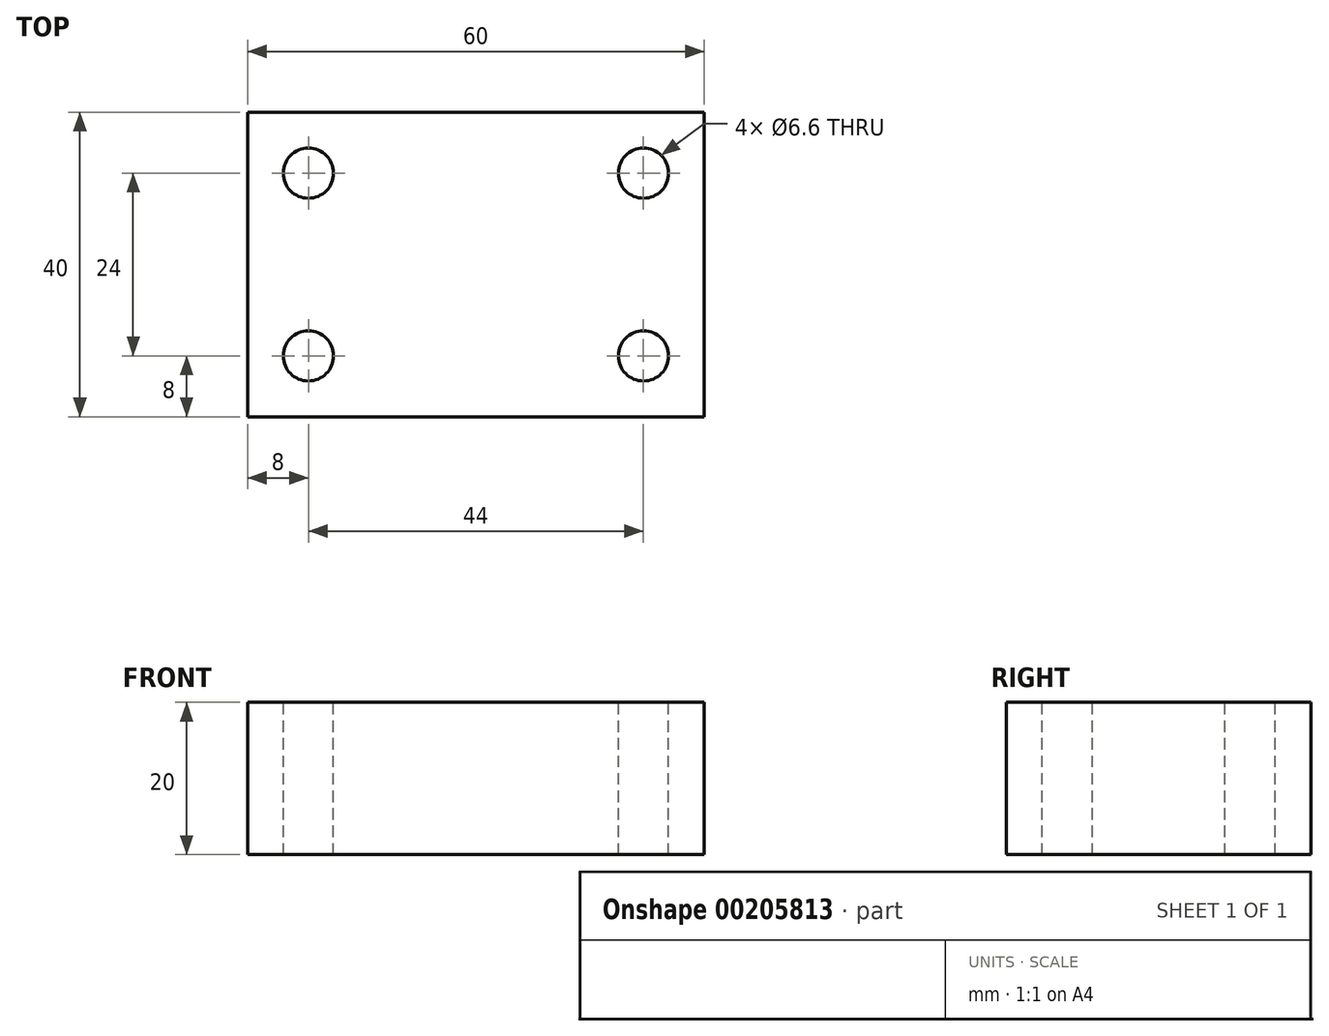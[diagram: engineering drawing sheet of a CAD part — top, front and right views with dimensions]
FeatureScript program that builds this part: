
annotation { "Feature Type Name" : "Feature", "Feature Type Description" : "" }
export const myFeature = defineFeature(function(context is Context, id is Id, definition is map)
    precondition{}
    {
        {
            var Q0;
            Q0=qCreatedBy(makeId("Top.planeOp"),FACE);
            var sketch = newSketch(context, id + "F0", { "sketchPlane" : qUnion([Q0])});
            skLineSegment(sketch, "E0.bottom", {"start": v(15, 10) * mm, "end": v(-15, 10) * mm});
            skLineSegment(sketch, "E0.top", {"start": v(15, -10) * mm, "end": v(-15, -10) * mm});
            skLineSegment(sketch, "E0.left", {"start": v(15, 10) * mm, "end": v(15, -10) * mm});
            skLineSegment(sketch, "E0.right", {"start": v(-15, 10) * mm, "end": v(-15, -10) * mm});
            skPoint(sketch, "E0.middle", {"position": v(0, 0) * mm});
            skSolve(sketch);
        }
        {
            var Q0;
            Q0=makeQuery(id+"F0.imprint","IMPRINT",FACE,{"disambiguationData":[TD([[makeQuery(id+"F0.imprint","IMPRINT",EDGE,{"derivedFrom":sQuery(id+"F0.wireOp",EDGE,"E0.bottom")}),1.0]])]});
            extrude(context, id + "F1", {"entities" : qUnion([Q0]), "depth" : 20 * mm});
        }
        {
            var Q0;
            Q0=makeQuery(id+"F1.opExtrude","CAP_FACE",FACE,{"disambiguationData":[OSD([sQuery(id+"F0.wireOp",EDGE,"E0.bottom"),sQuery(id+"F0.wireOp",EDGE,"E0.top"),sQuery(id+"F0.wireOp",EDGE,"E0.left"),sQuery(id+"F0.wireOp",EDGE,"E0.right")])],"isStart":false});
            var sketch = newSketch(context, id + "F2", { "sketchPlane" : qUnion([Q0])});
            skPoint(sketch, "E1", {"position": v(-7, 2) * mm});
            skSolve(sketch);
        }
        {
            var Q0;
            Q0=sQuery(id+"F2.wireOp",VERTEX,"E1");
            var Q1;
            Q1=makeQuery(id+"F1.opExtrude","SWEPT_BODY",BODY,{"disambiguationData":[OSD([sQuery(id+"F0.wireOp",EDGE,"E0.bottom"),sQuery(id+"F0.wireOp",EDGE,"E0.top"),sQuery(id+"F0.wireOp",EDGE,"E0.left"),sQuery(id+"F0.wireOp",EDGE,"E0.right")])]});
            hole(context, id + "F3", {"style" : HoleStyle.SIMPLE, "endStyle" : HoleEndStyle.THROUGH, "holeDiameter" : 6.6 * mm, "locations" : qUnion([Q0]), "scope" : qUnion([Q1]), "isTappedThrough" : true});
        }
        {
            var Q0;
            Q0=makeQuery(id+"F1.opExtrude","SWEPT_BODY",BODY,{"disambiguationData":[OSD([sQuery(id+"F0.wireOp",EDGE,"E0.bottom"),sQuery(id+"F0.wireOp",EDGE,"E0.top"),sQuery(id+"F0.wireOp",EDGE,"E0.left"),sQuery(id+"F0.wireOp",EDGE,"E0.right")])]});
            var Q1;
            Q1=makeQuery(id+"F1.opExtrude","SWEPT_FACE",FACE,{"disambiguationData":[OSD([sQuery(id+"F0.wireOp",EDGE,"E0.left")])]});
            mirror(context, id + "F4", {"operationType" : NewBodyOperationType.ADD, "entities" : qUnion([Q0]), "mirrorPlane" : qUnion([Q1])});
        }
        {
            var Q0;
            Q0=makeQuery(id+"F1.opExtrude","SWEPT_BODY",BODY,{"disambiguationData":[OSD([sQuery(id+"F0.wireOp",EDGE,"E0.bottom"),sQuery(id+"F0.wireOp",EDGE,"E0.top"),sQuery(id+"F0.wireOp",EDGE,"E0.left"),sQuery(id+"F0.wireOp",EDGE,"E0.right")])]});
            var Q1;
            {var subQ0=makeQuery(id+"F1.opExtrude","SWEPT_FACE",FACE,{"disambiguationData":[OSD([sQuery(id+"F0.wireOp",EDGE,"E0.top")])]});Q1=makeQuery(id+"F4.boolean.opBoolean","MERGE",FACE,{"derivedFrom":[subQ0,makeQuery(id+"F4.opPattern","COPY",FACE,{"derivedFrom":subQ0,"instanceName":"1"})]});}
            mirror(context, id + "F5", {"operationType" : NewBodyOperationType.ADD, "entities" : qUnion([Q0]), "mirrorPlane" : qUnion([Q1])});
        }
    });
